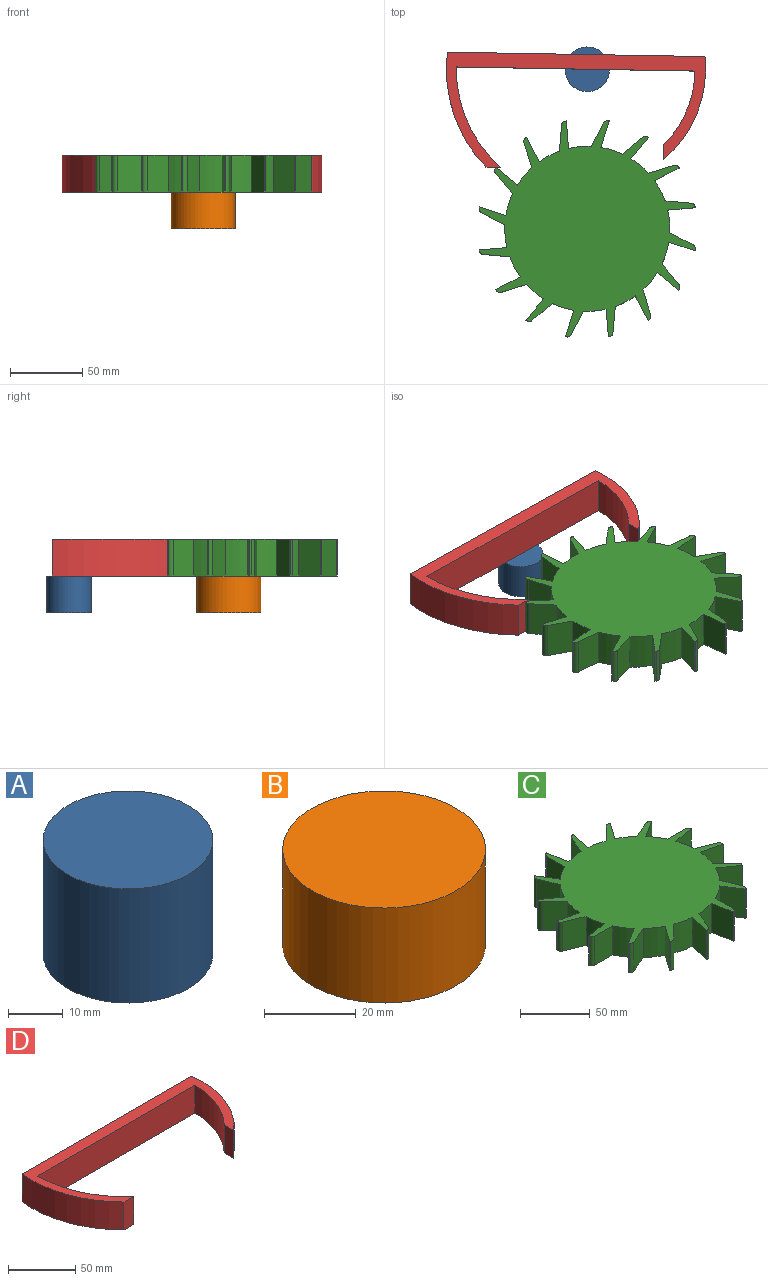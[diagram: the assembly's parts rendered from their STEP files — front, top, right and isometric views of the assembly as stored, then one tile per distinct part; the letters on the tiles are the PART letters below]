
ASSEMBLY  parts=4 mates=2
PART A: 3 faces, bbox 30.9x30.9x25.4 mm
  f0: cylinder r=15.44mm len=30.89mm, axis (0,0,1), area 2464.6mm2, adj f1,f2
  f1: plane 30.89x30.89mm, normal (0,0,-1), area 749.2mm2, adj f0
  f2: plane 30.89x30.89mm, normal (0,0,1), area 749.2mm2, adj f0
PART B: 3 faces, bbox 44.3x44.3x25.4 mm
  f0: cylinder r=22.17mm len=44.33mm, axis (0,0,1), area 3537.6mm2, adj f1,f2
  f1: plane 44.33x44.33mm, normal (0,0,-1), area 1543.6mm2, adj f0
  f2: plane 44.33x44.33mm, normal (0,0,1), area 1543.6mm2, adj f0
PART C: 82 faces, bbox 151.7x151.7x25.4 mm
  f0: cylinder r=57.15mm len=25.4mm, axis (0,0,-1), area 400.6mm2, adj f20,f21,f25,f29
  f1: cylinder r=57.15mm len=25.4mm, axis (0,0,-1), area 400.6mm2, adj f20,f21,f28,f33
  f2: cylinder r=57.15mm len=25.4mm, axis (0,0,-1), area 400.6mm2, adj f20,f21,f32,f37
  f3: cylinder r=57.15mm len=25.4mm, axis (0,0,-1), area 400.6mm2, adj f20,f21,f36,f41
  f4: cylinder r=57.15mm len=25.4mm, axis (0,0,-1), area 400.6mm2, adj f20,f21,f40,f45
  f5: cylinder r=57.15mm len=25.4mm, axis (0,0,-1), area 400.6mm2, adj f20,f21,f44,f49
  f6: cylinder r=57.15mm len=25.4mm, axis (0,0,-1), area 400.6mm2, adj f20,f21,f48,f53
  f7: cylinder r=57.15mm len=25.4mm, axis (0,0,-1), area 400.6mm2, adj f20,f21,f52,f57
  f8: cylinder r=57.15mm len=25.4mm, axis (0,0,-1), area 400.6mm2, adj f20,f21,f56,f61
  f9: cylinder r=57.15mm len=25.4mm, axis (0,0,-1), area 400.6mm2, adj f20,f21,f60,f65
  f10: cylinder r=57.15mm len=25.4mm, axis (0,0,-1), area 400.6mm2, adj f20,f21,f64,f69
  f11: cylinder r=57.15mm len=25.4mm, axis (0,0,-1), area 400.6mm2, adj f20,f21,f68,f73
  f12: cylinder r=57.15mm len=25.4mm, axis (0,0,-1), area 400.6mm2, adj f20,f21,f72,f77
  f13: cylinder r=57.15mm len=25.4mm, axis (0,0,-1), area 400.6mm2, adj f20,f21,f76,f80
  f14: cylinder r=57.15mm len=25.4mm, axis (0,0,-1), area 400.6mm2, adj f17,f20,f21,f81
  f15: plane 25.4x0.76mm, normal (0.95,0.3,0), area 20.2mm2, adj f16,f19,f20,f21
  f16: cylinder r=3mm len=25.4mm, axis (0,0,-1), area 96.6mm2, adj f15,f17,f20,f21
  f17: plane 25.4x18.27mm, normal (0,1,0), area 464.1mm2, adj f14,f16,f20,f21
  f18: cylinder r=57.15mm len=25.4mm, axis (0,0,-1), area 400.6mm2, adj f19,f20,f21,f24
  f19: plane 25.4x18.91mm, normal (0.17,-0.98,0), area 487.7mm2, adj f15,f18,f20,f21
  f20: plane 151.65x151.65mm, normal (0,0,1), area 11711.6mm2, adj f0,f1,f2,f3,f4,f5,f6,f7
  f21: plane 151.65x151.65mm, normal (0,0,-1), area 11711.6mm2, adj f0,f1,f2,f3,f4,f5,f6,f7
  f22: plane 25.4x0.79mm, normal (1,-0.09,0), area 20.2mm2, adj f20,f21,f23,f25
  f23: cylinder r=3mm len=25.4mm, axis (0,0,-1), area 96.6mm2, adj f20,f21,f22,f24
  f24: plane 25.4x16.88mm, normal (0.38,0.92,0), area 464.1mm2, adj f18,f20,f21,f23
  f25: plane 25.4x18.75mm, normal (-0.22,-0.98,0), area 487.7mm2, adj f0,f20,f21,f22
  f26: plane 25.4x0.7mm, normal (0.89,-0.46,0), area 20.2mm2, adj f20,f21,f27,f28
  f27: cylinder r=3mm len=25.4mm, axis (0,0,-1), area 96.6mm2, adj f20,f21,f26,f29
  f28: plane 25.4x15.73mm, normal (-0.57,-0.82,0), area 487.7mm2, adj f1,f20,f21,f26
  f29: plane 25.4x12.92mm, normal (0.71,0.71,0), area 464.1mm2, adj f0,f20,f21,f27
  f30: plane 25.4x0.61mm, normal (0.64,-0.77,0), area 20.2mm2, adj f20,f21,f31,f32
  f31: cylinder r=3mm len=25.4mm, axis (0,0,-1), area 96.6mm2, adj f20,f21,f30,f33
  f32: plane 25.4x16.19mm, normal (-0.84,-0.54,0), area 487.7mm2, adj f2,f20,f21,f30
  f33: plane 25.4x16.88mm, normal (0.92,0.38,0), area 464.1mm2, adj f1,f20,f21,f31
  f34: plane 25.4x0.76mm, normal (0.3,-0.95,0), area 20.2mm2, adj f20,f21,f35,f36
  f35: cylinder r=3mm len=25.4mm, axis (0,0,-1), area 96.6mm2, adj f20,f21,f34,f37
  f36: plane 25.4x18.91mm, normal (-0.98,-0.17,0), area 487.7mm2, adj f3,f20,f21,f34
  f37: plane 25.4x18.27mm, normal (1,0,0), area 464.1mm2, adj f2,f20,f21,f35
  f38: plane 25.4x0.79mm, normal (-0.09,-1,0), area 20.2mm2, adj f20,f21,f39,f40
  f39: cylinder r=3mm len=25.4mm, axis (0,0,-1), area 96.6mm2, adj f20,f21,f38,f41
  f40: plane 25.4x18.75mm, normal (-0.98,0.22,0), area 487.7mm2, adj f4,f20,f21,f38
  f41: plane 25.4x16.88mm, normal (0.92,-0.38,0), area 464.1mm2, adj f3,f20,f21,f39
  f42: plane 25.4x0.7mm, normal (-0.46,-0.89,0), area 20.2mm2, adj f20,f21,f43,f44
  f43: cylinder r=3mm len=25.4mm, axis (0,0,-1), area 96.6mm2, adj f20,f21,f42,f45
  f44: plane 25.4x15.73mm, normal (-0.82,0.57,0), area 487.7mm2, adj f5,f20,f21,f42
  f45: plane 25.4x12.92mm, normal (0.71,-0.71,0), area 464.1mm2, adj f4,f20,f21,f43
  f46: plane 25.4x0.61mm, normal (-0.77,-0.64,0), area 20.2mm2, adj f20,f21,f47,f48
  f47: cylinder r=3mm len=25.4mm, axis (0,0,-1), area 96.6mm2, adj f20,f21,f46,f49
  f48: plane 25.4x16.19mm, normal (-0.54,0.84,0), area 487.7mm2, adj f6,f20,f21,f46
  f49: plane 25.4x16.88mm, normal (0.38,-0.92,0), area 464.1mm2, adj f5,f20,f21,f47
  f50: plane 25.4x0.76mm, normal (-0.95,-0.3,0), area 20.2mm2, adj f20,f21,f51,f52
  f51: cylinder r=3mm len=25.4mm, axis (0,0,-1), area 96.6mm2, adj f20,f21,f50,f53
  f52: plane 25.4x18.91mm, normal (-0.17,0.98,0), area 487.7mm2, adj f7,f20,f21,f50
  f53: plane 25.4x18.27mm, normal (0,-1,0), area 464.1mm2, adj f6,f20,f21,f51
  f54: plane 25.4x0.79mm, normal (-1,0.09,0), area 20.2mm2, adj f20,f21,f55,f56
  f55: cylinder r=3mm len=25.4mm, axis (0,0,-1), area 96.6mm2, adj f20,f21,f54,f57
  f56: plane 25.4x18.75mm, normal (0.22,0.98,0), area 487.7mm2, adj f8,f20,f21,f54
  f57: plane 25.4x16.88mm, normal (-0.38,-0.92,0), area 464.1mm2, adj f7,f20,f21,f55
  f58: plane 25.4x0.7mm, normal (-0.89,0.46,0), area 20.2mm2, adj f20,f21,f59,f60
  f59: cylinder r=3mm len=25.4mm, axis (0,0,-1), area 96.6mm2, adj f20,f21,f58,f61
  f60: plane 25.4x15.73mm, normal (0.57,0.82,0), area 487.7mm2, adj f9,f20,f21,f58
  f61: plane 25.4x12.92mm, normal (-0.71,-0.71,0), area 464.1mm2, adj f8,f20,f21,f59
  f62: plane 25.4x0.61mm, normal (-0.64,0.77,0), area 20.2mm2, adj f20,f21,f63,f64
  f63: cylinder r=3mm len=25.4mm, axis (0,0,-1), area 96.6mm2, adj f20,f21,f62,f65
  f64: plane 25.4x16.19mm, normal (0.84,0.54,0), area 487.7mm2, adj f10,f20,f21,f62
  f65: plane 25.4x16.88mm, normal (-0.92,-0.38,0), area 464.1mm2, adj f9,f20,f21,f63
  f66: plane 25.4x0.76mm, normal (-0.3,0.95,0), area 20.2mm2, adj f20,f21,f67,f68
  f67: cylinder r=3mm len=25.4mm, axis (0,0,-1), area 96.6mm2, adj f20,f21,f66,f69
  f68: plane 25.4x18.91mm, normal (0.98,0.17,0), area 487.7mm2, adj f11,f20,f21,f66
  f69: plane 25.4x18.27mm, normal (-1,0,0), area 464.1mm2, adj f10,f20,f21,f67
  f70: plane 25.4x0.79mm, normal (0.09,1,0), area 20.2mm2, adj f20,f21,f71,f72
  f71: cylinder r=3mm len=25.4mm, axis (0,0,-1), area 96.6mm2, adj f20,f21,f70,f73
  f72: plane 25.4x18.75mm, normal (0.98,-0.22,0), area 487.7mm2, adj f12,f20,f21,f70
  f73: plane 25.4x16.88mm, normal (-0.92,0.38,0), area 464.1mm2, adj f11,f20,f21,f71
  f74: plane 25.4x0.7mm, normal (0.46,0.89,0), area 20.2mm2, adj f20,f21,f75,f76
  f75: cylinder r=3mm len=25.4mm, axis (0,0,-1), area 96.6mm2, adj f20,f21,f74,f77
  f76: plane 25.4x15.73mm, normal (0.82,-0.57,0), area 487.7mm2, adj f13,f20,f21,f74
  f77: plane 25.4x12.92mm, normal (-0.71,0.71,0), area 464.1mm2, adj f12,f20,f21,f75
  f78: plane 25.4x0.61mm, normal (0.77,0.64,0), area 20.2mm2, adj f20,f21,f79,f81
  f79: cylinder r=3mm len=25.4mm, axis (0,0,-1), area 96.6mm2, adj f20,f21,f78,f80
  f80: plane 25.4x16.88mm, normal (-0.38,0.92,0), area 464.1mm2, adj f13,f20,f21,f79
  f81: plane 25.4x16.19mm, normal (0.54,-0.84,0), area 487.7mm2, adj f14,f20,f21,f78
PART D: 10 faces, bbox 179.5x79.2x25.4 mm
  f0: cylinder r=74.56mm len=51.54mm, axis (0,0,-1), area 1445.4mm2, adj f1,f7,f8,f9
  f1: plane 25.4x10.16mm, normal (-1,0,0), area 258.1mm2, adj f0,f2,f8,f9
  f2: cylinder r=81.91mm len=71.86mm, axis (0,0,-1), area 2033.4mm2, adj f1,f3,f8,f9
  f3: plane 178.32x25.4mm, normal (0,1,0), area 4529.4mm2, adj f2,f4,f8,f9
  f4: cylinder r=97.57mm len=79.16mm, axis (0,0,-1), area 2205.2mm2, adj f3,f5,f8,f9
  f5: plane 25.4x10.16mm, normal (0,-1,0), area 258.1mm2, adj f4,f6,f8,f9
  f6: cylinder r=90.67mm len=69mm, axis (0,0,-1), area 1991.7mm2, adj f5,f7,f8,f9
  f7: plane 165.23x25.4mm, normal (0,-1,0), area 4197mm2, adj f0,f6,f8,f9
  f8: plane 179.49x79.16mm, normal (0,0,1), area 2820.5mm2, adj f0,f1,f2,f3,f4,f5,f6,f7
  f9: plane 179.49x79.16mm, normal (0,0,-1), area 2820.5mm2, adj f0,f1,f2,f3,f4,f5,f6,f7
PLACE A at identity fixed
PLACE B at identity fixed
PLACE C rot(axis=(0,0,1),84.8deg) t=(0,0,0)mm
PLACE D rot(axis=(0,0,-1),1deg) t=(-1.87,0.02,0)mm
MATE revolute C.f0 <-> B.f0  axis (0,0,-1) through (0,0,0)mm
MATE revolute A.f0 <-> D.f2  axis (0,0,1) through (0,110.5,0)mm
